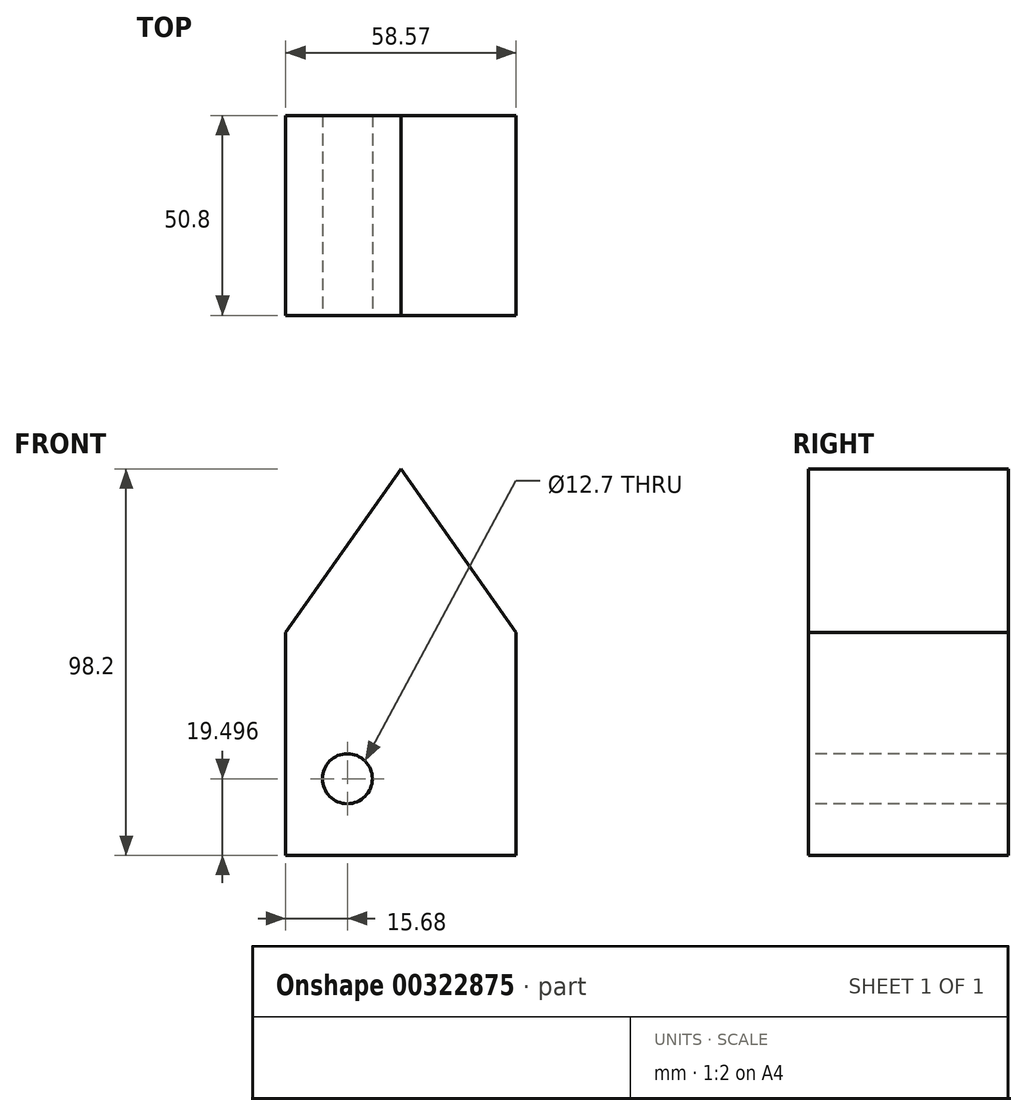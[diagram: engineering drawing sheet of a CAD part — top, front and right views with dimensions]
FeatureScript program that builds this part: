
annotation { "Feature Type Name" : "Feature", "Feature Type Description" : "" }
export const myFeature = defineFeature(function(context is Context, id is Id, definition is map)
    precondition{}
    {
        {
            var Q0;
            Q0=qCreatedBy(makeId("Front.planeOp"),FACE);
            var sketch = newSketch(context, id + "F0", { "sketchPlane" : qUnion([Q0])});
            skLineSegment(sketch, "E0.top", {"start": v(-15.68, -32.48) * mm, "end": v(42.89, -32.48) * mm});
            skLineSegment(sketch, "E0.left", {"start": v(-15.68, 24.21) * mm, "end": v(-15.68, -32.48) * mm});
            skLineSegment(sketch, "E0.right", {"start": v(42.89, 24.21) * mm, "end": v(42.89, -32.48) * mm});
            skLineSegment(sketch, "E1", {"start": v(-15.68, 24.21) * mm, "end": v(13.6, 65.72) * mm});
            skLineSegment(sketch, "E2", {"start": v(42.89, 24.21) * mm, "end": v(13.6, 65.72) * mm});
            skCircle(sketch, "E3", {"center": v(0, -12.98) * mm, "radius": 6.35 * mm});
            skSolve(sketch);
        }
        {
            var Q0;
            Q0=makeQuery(id+"F0.imprint","IMPRINT",FACE,{"disambiguationData":[TD([[makeQuery(id+"F0.imprint","IMPRINT",EDGE,{"derivedFrom":sQuery(id+"F0.wireOp",EDGE,"E0.top")}),1.0]])]});
            extrude(context, id + "F1", {"entities" : qUnion([Q0]), "oppositeDirection" : true, "depth" : 50.8 * mm});
        }
    });
